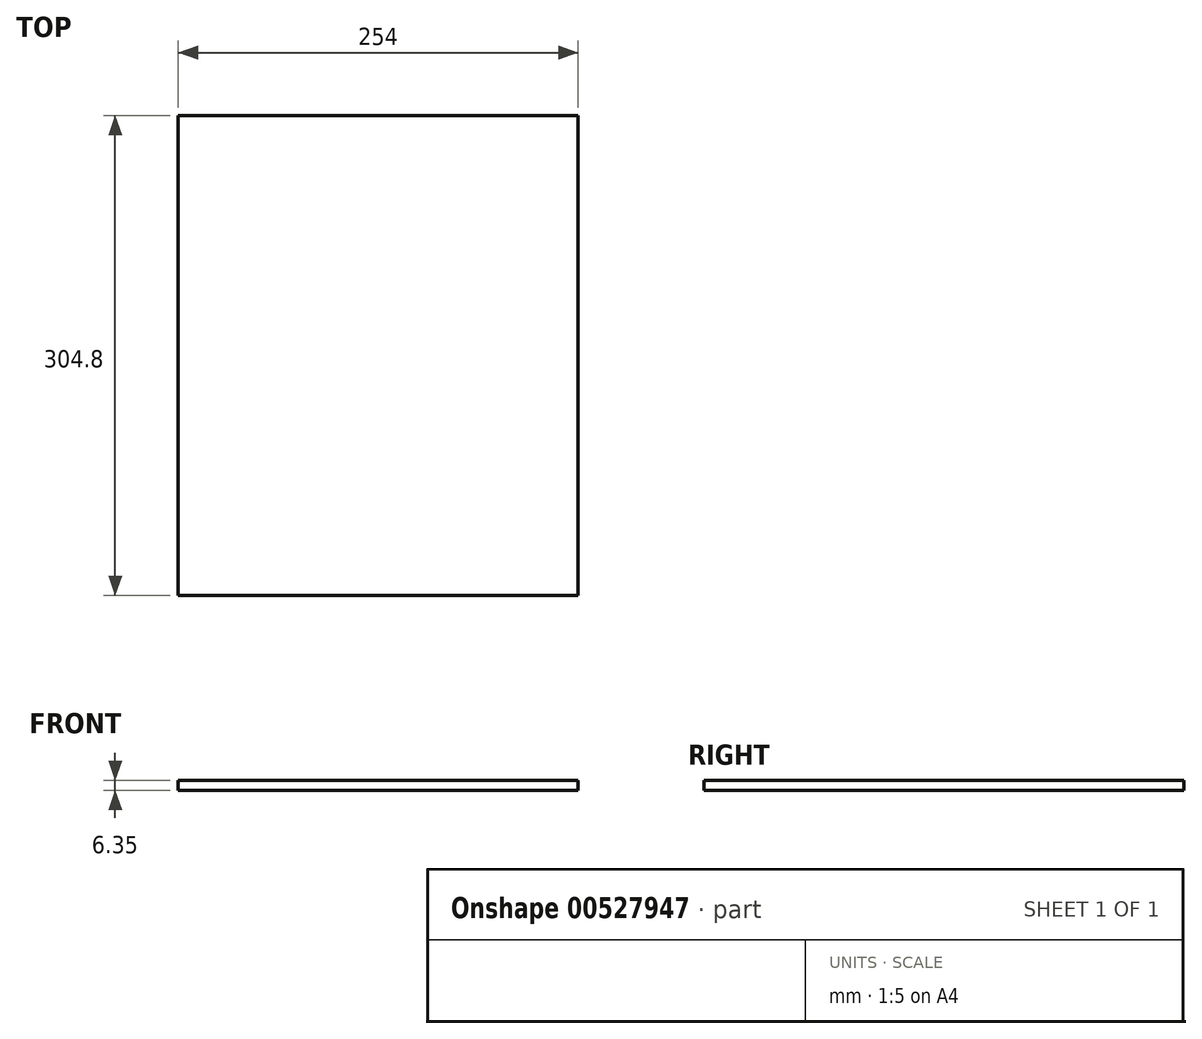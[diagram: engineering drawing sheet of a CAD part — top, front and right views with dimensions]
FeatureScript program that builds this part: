
annotation { "Feature Type Name" : "Feature", "Feature Type Description" : "" }
export const myFeature = defineFeature(function(context is Context, id is Id, definition is map)
    precondition{}
    {
        {
            var Q0;
            Q0=qCreatedBy(makeId("Top.planeOp"),FACE);
            var sketch = newSketch(context, id + "F0", { "sketchPlane" : qUnion([Q0])});
            skLineSegment(sketch, "E0.bottom", {"start": v(-127, 152.4) * mm, "end": v(127, 152.4) * mm});
            skLineSegment(sketch, "E0.top", {"start": v(-127, -152.4) * mm, "end": v(127, -152.4) * mm});
            skLineSegment(sketch, "E0.left", {"start": v(-127, 152.4) * mm, "end": v(-127, -152.4) * mm});
            skLineSegment(sketch, "E0.right", {"start": v(127, 152.4) * mm, "end": v(127, -152.4) * mm});
            skPoint(sketch, "E0.middle", {"position": v(0, 0) * mm});
            skSolve(sketch);
        }
        {
            var Q0;
            Q0 = qSketchRegion(id + "F0", true);
            extrude(context, id + "F1", {"entities" : qUnion([Q0]), "depth" : 6.35 * mm, "offsetDistance" : 25.4 * mm});
        }
    });
